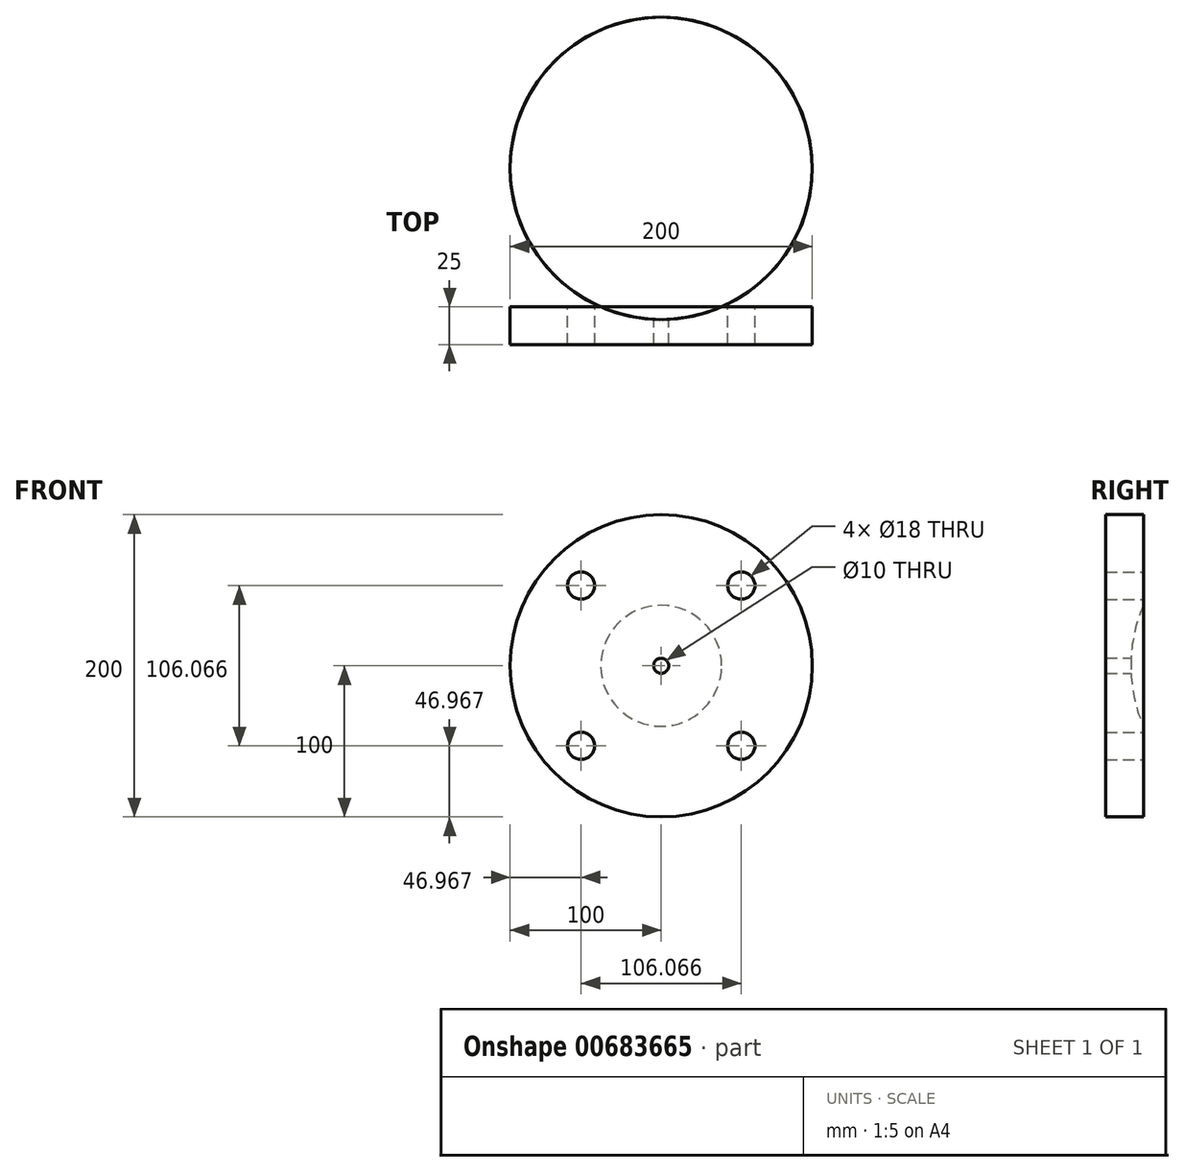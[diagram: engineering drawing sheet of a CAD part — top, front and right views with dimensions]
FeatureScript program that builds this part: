
annotation { "Feature Type Name" : "Feature", "Feature Type Description" : "" }
export const myFeature = defineFeature(function(context is Context, id is Id, definition is map)
    precondition{}
    {
        {
            var Q0;
            Q0=qCreatedBy(makeId("Front.planeOp"),FACE);
            var sketch = newSketch(context, id + "F0", { "sketchPlane" : qUnion([Q0])});
            skCircle(sketch, "E0", {"center": v(0, 0) * mm, "radius": 100 * mm});
            skLineSegment(sketch, "E1", {"start": v(0, 0) * mm, "end": v(-53.03, 53.03) * mm, "construction": true});
            skCircle(sketch, "E2", {"center": v(-53.03, 53.03) * mm, "radius": 9 * mm});
            skCircle(sketch, "E3.MirrorC", {"center": v(53.03, 53.03) * mm, "radius": 9 * mm});
            skCircle(sketch, "E4.MirrorC", {"center": v(53.03, -53.03) * mm, "radius": 9 * mm});
            skCircle(sketch, "E5.MirrorC", {"center": v(-53.03, -53.03) * mm, "radius": 9 * mm});
            skCircle(sketch, "E6", {"center": v(0, 0) * mm, "radius": 5 * mm});
            skSolve(sketch);
        }
        {
            var Q0;
            Q0=makeQuery(id+"F0.imprint","IMPRINT",FACE,{"disambiguationData":[TD([[makeQuery(id+"F0.imprint","IMPRINT",EDGE,{"derivedFrom":sQuery(id+"F0.wireOp",EDGE,"E0")}),1.0]])]});
            extrude(context, id + "F1", {"entities" : qUnion([Q0]), "depth" : 25 * mm, "offsetDistance" : 25 * mm});
        }
        {
            var Q0;
            Q0=qCreatedBy(makeId("Right.planeOp"),FACE);
            var sketch = newSketch(context, id + "F2", { "sketchPlane" : qUnion([Q0])});
            skArc(sketch, "E7", {"start": v(91.65, 100) * mm, "mid": v(-8.35, 0) * mm, "end": v(91.65, -100) * mm});
            skLineSegment(sketch, "E8.0", {"start": v(0, -40) * mm, "end": v(0, 40) * mm});
            skPoint(sketch, "E9.orphan", {"position": v(0, 100) * mm});
            skPoint(sketch, "E10.orphan", {"position": v(0, -100) * mm});
            skLineSegment(sketch, "E11", {"start": v(91.65, 0) * mm, "end": v(91.65, 100) * mm});
            skLineSegment(sketch, "E12", {"start": v(91.65, 0) * mm, "end": v(91.65, -100) * mm});
            skSolve(sketch);
        }
        {
            var Q0;
            {var subQ0=sQuery(id+"F2.wireOp",EDGE,"E8.0");Q0=makeQuery(id+"F2.imprint","IMPRINT",FACE,{"disambiguationData":[TD([[makeQuery(id+"F2.imprint","IMPRINT",EDGE,{"derivedFrom":subQ0}),1.0]])]});}
            var Q1;
            Q1=sQuery(id+"F2.wireOp",EDGE,"E11");
            revolve(context, id + "F3", {"operationType" : NewBodyOperationType.REMOVE, "entities" : qUnion([Q0]), "axis" : qUnion([Q1]), "revolveType" : RevolveType.FULL, "oppositeDirection" : true});
        }
    });
